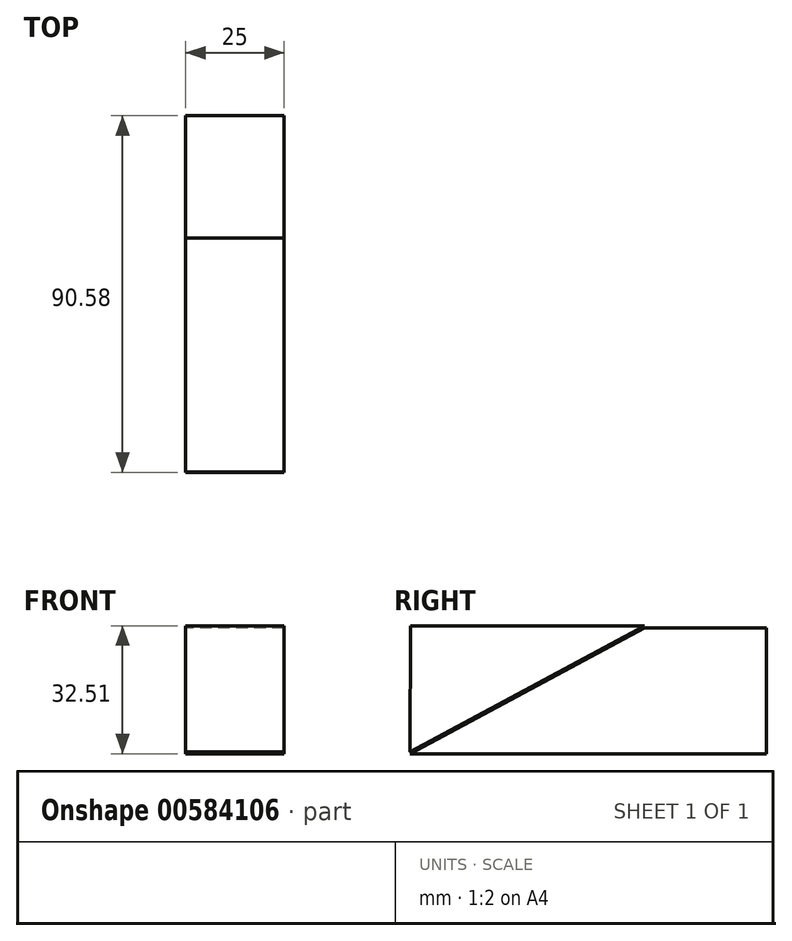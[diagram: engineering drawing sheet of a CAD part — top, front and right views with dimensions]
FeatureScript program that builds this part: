
annotation { "Feature Type Name" : "Feature", "Feature Type Description" : "" }
export const myFeature = defineFeature(function(context is Context, id is Id, definition is map)
    precondition{}
    {
        {
            var Q0;
            Q0=qCreatedBy(makeId("Right.planeOp"),FACE);
            var sketch = newSketch(context, id + "F0", { "sketchPlane" : qUnion([Q0])});
            skLineSegment(sketch, "E0", {"start": v(-66.55, 39.38) * mm, "end": v(-7.11, 39.38) * mm});
            skLineSegment(sketch, "E1", {"start": v(-7.11, 39.38) * mm, "end": v(-66.62, 7.35) * mm});
            skLineSegment(sketch, "E2", {"start": v(-66.62, 7.35) * mm, "end": v(-66.55, 39.38) * mm});
            skSolve(sketch);
        }
        {
            var Q0;
            Q0=makeQuery(id+"F0.imprint","IMPRINT",FACE,{"disambiguationData":[TD([[makeQuery(id+"F0.imprint","IMPRINT",EDGE,{"derivedFrom":sQuery(id+"F0.wireOp",EDGE,"E0")}),-1.0]])]});
            extrude(context, id + "F1", {"entities" : qUnion([Q0]), "depth" : 25 * mm, "offsetDistance" : 25 * mm});
        }
        {
            var Q0;
            Q0=qCreatedBy(makeId("Right.planeOp"),FACE);
            var sketch = newSketch(context, id + "F2", { "sketchPlane" : qUnion([Q0])});
            skLineSegment(sketch, "E3", {"start": v(-66.62, 6.87) * mm, "end": v(23.96, 6.87) * mm});
            skLineSegment(sketch, "E4", {"start": v(23.96, 6.87) * mm, "end": v(23.96, 38.9) * mm});
            skLineSegment(sketch, "E5", {"start": v(23.96, 38.9) * mm, "end": v(-7.11, 38.9) * mm});
            skLineSegment(sketch, "E6", {"start": v(-7.11, 38.9) * mm, "end": v(-66.62, 6.87) * mm});
            skSolve(sketch);
        }
        {
            var Q0;
            Q0 = qSketchRegion(id + "F2", true);
            extrude(context, id + "F3", {"entities" : qUnion([Q0]), "depth" : 25 * mm, "offsetDistance" : 25 * mm});
        }
    });
